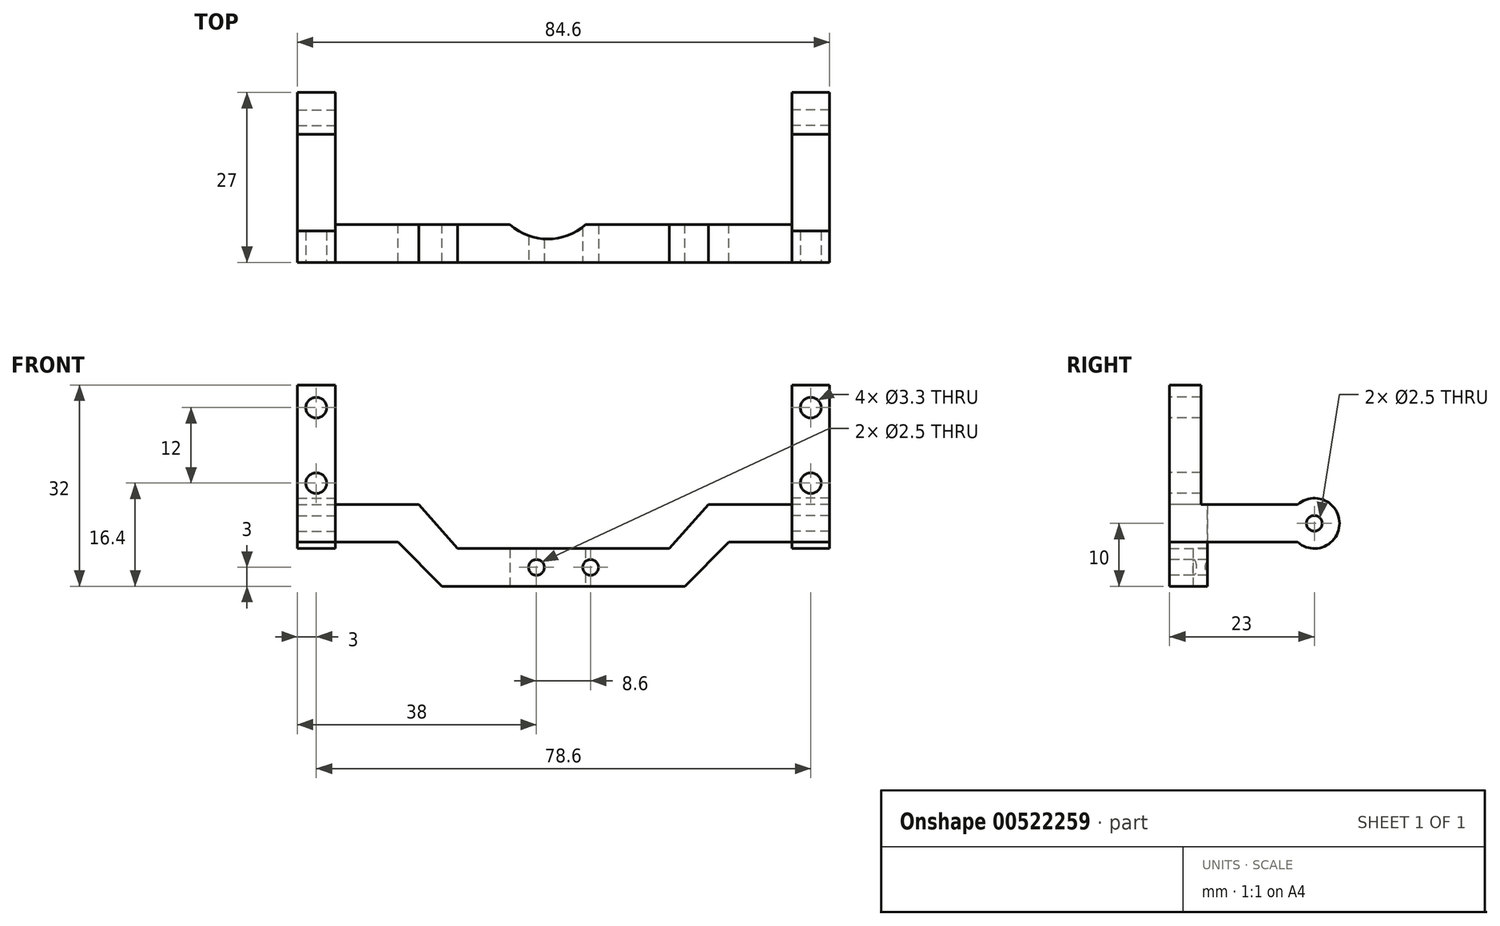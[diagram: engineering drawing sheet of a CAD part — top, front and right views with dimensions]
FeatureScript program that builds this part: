
annotation { "Feature Type Name" : "Feature", "Feature Type Description" : "" }
export const myFeature = defineFeature(function(context is Context, id is Id, definition is map)
    precondition{}
    {
        {
            var Q0;
            Q0=qCreatedBy(makeId("Top.planeOp"),FACE);
            var sketch = newSketch(context, id + "F0", { "sketchPlane" : qUnion([Q0])});
            skLineSegment(sketch, "E0.bottom", {"start": v(-33.8, 3) * mm, "end": v(38.8, 3) * mm});
            skLineSegment(sketch, "E0.top", {"start": v(-33.8, -3) * mm, "end": v(-6, -3) * mm});
            skLineSegment(sketch, "E0.left", {"start": v(-33.8, 3) * mm, "end": v(-33.8, -3) * mm});
            skLineSegment(sketch, "E0.right", {"start": v(38.8, 3) * mm, "end": v(38.8, -3) * mm});
            skLineSegment(sketch, "E1.trimOffspring", {"start": v(6, -3) * mm, "end": v(38.8, -3) * mm});
            skLineSegment(sketch, "E2", {"start": v(-6, -3) * mm, "end": v(6, -3) * mm});
            skSolve(sketch);
        }
        {
            var Q0;
            Q0=makeQuery(id+"F0.imprint","IMPRINT",FACE,{"disambiguationData":[TD([[makeQuery(id+"F0.imprint","IMPRINT",EDGE,{"derivedFrom":sQuery(id+"F0.wireOp",EDGE,"E0.bottom")}),-1.0]])]});
            extrude(context, id + "F1", {"entities" : qUnion([Q0]), "depth" : 13 * mm, "offsetDistance" : 25 * mm});
        }
        {
            var Q0;
            Q0=makeQuery(id+"F1.opExtrude","SWEPT_FACE",FACE,{"disambiguationData":[OSD([sQuery(id+"F0.wireOp",EDGE,"E0.bottom")])]});
            var sketch = newSketch(context, id + "F2", { "sketchPlane" : qUnion([Q0])});
            skLineSegment(sketch, "E3", {"start": v(-38.8, 0) * mm, "end": v(33.8, 0) * mm});
            skLineSegment(sketch, "E4", {"start": v(33.8, 0) * mm, "end": v(33.8, 13) * mm});
            skLineSegment(sketch, "E5", {"start": v(33.8, 13) * mm, "end": v(-38.8, 13) * mm});
            skLineSegment(sketch, "E6", {"start": v(-38.8, 13) * mm, "end": v(-38.8, 0) * mm});
            skLineSegment(sketch, "E7", {"start": v(-38.8, 7) * mm, "end": v(-28.8, 7) * mm});
            skLineSegment(sketch, "E8", {"start": v(-28.8, 7) * mm, "end": v(-28.8, 0) * mm});
            skLineSegment(sketch, "E9", {"start": v(23.8, 7) * mm, "end": v(23.8, 0) * mm});
            skLineSegment(sketch, "E10", {"start": v(-28.8, 7) * mm, "end": v(-21.8, 0) * mm});
            skLineSegment(sketch, "E11", {"start": v(23.8, 7) * mm, "end": v(16.8, 0) * mm});
            skLineSegment(sketch, "E12.trimOffspring", {"start": v(23.8, 7) * mm, "end": v(33.8, 7) * mm});
            skLineSegment(sketch, "E13.0", {"start": v(-24.56, 11.24) * mm, "end": v(-20.28, 6.97) * mm});
            skLineSegment(sketch, "E14.0", {"start": v(19.56, 11.24) * mm, "end": v(14.31, 6) * mm});
            skLineSegment(sketch, "E15", {"start": v(-19.31, 6) * mm, "end": v(14.31, 6) * mm});
            skPoint(sketch, "E15.startSnap0", {"position": v(-20.28, 6.97) * mm});
            skPoint(sketch, "E16.orphan", {"position": v(-27.25, 13.94) * mm});
            skPoint(sketch, "E17.orphan", {"position": v(-19.34, -2.46) * mm});
            skPoint(sketch, "E18.orphan", {"position": v(14.34, -2.46) * mm});
            skPoint(sketch, "E19.orphan", {"position": v(6.71, 0) * mm});
            skLineSegment(sketch, "E20.trimOffspring", {"start": v(-19.31, 6) * mm, "end": v(-25.51, 13) * mm});
            skPoint(sketch, "E21.end.orphan", {"position": v(-13.31, 0) * mm});
            skLineSegment(sketch, "E22.trimOffspring", {"start": v(14.31, 6) * mm, "end": v(20.51, 13) * mm});
            skPoint(sketch, "E23.orphan", {"position": v(-20.28, 6) * mm});
            skSolve(sketch);
        }
        {
            var Q0;
            {var subQ0=sQuery(id+"F2.wireOp",EDGE,"E8");Q0=makeQuery(id+"F2.imprint","IMPRINT",FACE,{"disambiguationData":[TD([[makeQuery(id+"F2.imprint","IMPRINT",EDGE,{"derivedFrom":subQ0}),1.0]])]});}
            var Q1;
            {var subQ4=sQuery(id+"F2.wireOp",EDGE,"E7");Q1=makeQuery(id+"F2.imprint","IMPRINT",FACE,{"disambiguationData":[TD([[makeQuery(id+"F2.imprint","IMPRINT",EDGE,{"derivedFrom":subQ4}),-1.0]])]});}
            var Q2;
            {var subQ3=sQuery(id+"F2.wireOp",EDGE,"E15");Q2=makeQuery(id+"F2.imprint","IMPRINT",FACE,{"disambiguationData":[TD([[makeQuery(id+"F2.imprint","IMPRINT",EDGE,{"derivedFrom":subQ3}),1.0]])]});}
            var Q3;
            {var subQ0=sQuery(id+"F2.wireOp",EDGE,"E9");Q3=makeQuery(id+"F2.imprint","IMPRINT",FACE,{"disambiguationData":[TD([[makeQuery(id+"F2.imprint","IMPRINT",EDGE,{"derivedFrom":subQ0}),-1.0]])]});}
            var Q4;
            {var subQ3=sQuery(id+"F2.wireOp",EDGE,"E9");Q4=makeQuery(id+"F2.imprint","IMPRINT",FACE,{"disambiguationData":[TD([[makeQuery(id+"F2.imprint","IMPRINT",EDGE,{"derivedFrom":subQ3}),1.0]])]});}
            extrude(context, id + "F3", {"entities" : qUnion([Q0, Q1, Q2, Q3, Q4]), "operationType" : NewBodyOperationType.REMOVE, "endBound" : BoundingType.THROUGH_ALL, "oppositeDirection" : true, "depth" : 25 * mm, "offsetDistance" : 25 * mm});
        }
        {
            var Q0;
            Q0=makeQuery(id+"F1.opExtrude","CAP_FACE",FACE,{"disambiguationData":[OSD([sQuery(id+"F0.wireOp",EDGE,"E0.bottom"),sQuery(id+"F0.wireOp",EDGE,"E0.top"),sQuery(id+"F0.wireOp",EDGE,"E0.left"),sQuery(id+"F0.wireOp",EDGE,"E0.right"),sQuery(id+"F0.wireOp",EDGE,"E1.trimOffspring"),sQuery(id+"F0.wireOp",EDGE,"E2")])],"isStart":true});
            var sketch = newSketch(context, id + "F4", { "sketchPlane" : qUnion([Q0])});
            skArc(sketch, "E24", {"start": v(6, -3) * mm, "mid": v(0, -0.7) * mm, "end": v(-6, -3) * mm});
            skSolve(sketch);
        }
        {
            var Q0;
            {var subQ0=sQuery(id+"F4.wireOp",EDGE,"E24");Q0=makeQuery(id+"F4.imprint","IMPRINT",FACE,{"disambiguationData":[TD([[makeQuery(id+"F4.imprint","IMPRINT",EDGE,{"derivedFrom":subQ0}),1.0]])]});}
            extrude(context, id + "F5", {"entities" : qUnion([Q0]), "operationType" : NewBodyOperationType.REMOVE, "endBound" : BoundingType.THROUGH_ALL, "oppositeDirection" : true, "depth" : 25 * mm, "offsetDistance" : 25 * mm});
        }
        {
            var Q0;
            Q0=makeQuery(id+"F1.opExtrude","SWEPT_FACE",FACE,{"disambiguationData":[OSD([sQuery(id+"F0.wireOp",EDGE,"E0.top"),sQuery(id+"F0.wireOp",EDGE,"E1.trimOffspring"),sQuery(id+"F0.wireOp",EDGE,"E2")])]});
            var sketch = newSketch(context, id + "F6", { "sketchPlane" : qUnion([Q0])});
            skCircle(sketch, "E25", {"center": v(-1.8, 3) * mm, "radius": 1.25 * mm});
            skCircle(sketch, "E26", {"center": v(6.8, 3) * mm, "radius": 1.25 * mm});
            skSolve(sketch);
        }
        {
            var Q0;
            Q0=makeQuery(id+"F6.imprint","IMPRINT",FACE,{"disambiguationData":[TD([[makeQuery(id+"F6.imprint","IMPRINT",EDGE,{"derivedFrom":sQuery(id+"F6.wireOp",EDGE,"E25")}),1.0]])]});
            var Q1;
            Q1=makeQuery(id+"F6.imprint","IMPRINT",FACE,{"disambiguationData":[TD([[makeQuery(id+"F6.imprint","IMPRINT",EDGE,{"derivedFrom":sQuery(id+"F6.wireOp",EDGE,"E26")}),1.0]])]});
            extrude(context, id + "F7", {"entities" : qUnion([Q0, Q1]), "operationType" : NewBodyOperationType.REMOVE, "endBound" : BoundingType.THROUGH_ALL, "oppositeDirection" : true, "depth" : 25 * mm, "offsetDistance" : 25 * mm});
        }
        {
            var Q0;
            Q0=makeQuery(id+"F1.opExtrude","SWEPT_FACE",FACE,{"disambiguationData":[OSD([sQuery(id+"F0.wireOp",EDGE,"E0.right")])]});
            var sketch = newSketch(context, id + "F8", { "sketchPlane" : qUnion([Q0])});
            skLineSegment(sketch, "E27", {"start": v(-3, 7) * mm, "end": v(-3, 32) * mm});
            skLineSegment(sketch, "E28", {"start": v(2, 32) * mm, "end": v(2, 13) * mm});
            skLineSegment(sketch, "E29", {"start": v(-3, 32) * mm, "end": v(2, 32) * mm});
            skLineSegment(sketch, "E30", {"start": v(2, 13) * mm, "end": v(17.35, 13) * mm});
            skLineSegment(sketch, "E31", {"start": v(17.35, 7) * mm, "end": v(3, 7) * mm});
            skPoint(sketch, "E32.orphan", {"position": v(-3, 31.12) * mm});
            skPoint(sketch, "E33.orphan", {"position": v(2, 31.12) * mm});
            skCircle(sketch, "E34", {"center": v(20, 10) * mm, "radius": 1.25 * mm});
            skPoint(sketch, "E34.centerSnap0", {"position": v(3, 10) * mm});
            skArc(sketch, "E35", {"start": v(17.35, 7) * mm, "mid": v(24, 10) * mm, "end": v(17.35, 13) * mm});
            skPoint(sketch, "E36.orphan", {"position": v(30, 7) * mm});
            skLineSegment(sketch, "E37", {"start": v(3, 7) * mm, "end": v(-3, 7) * mm});
            skLineSegment(sketch, "E38", {"start": v(-3, 13) * mm, "end": v(-3, 7) * mm});
            skLineSegment(sketch, "E39", {"start": v(2, 13) * mm, "end": v(3, 13) * mm});
            skSolve(sketch);
        }
        {
            var Q0;
            Q0=makeQuery(id+"F8.imprint","IMPRINT",FACE,{"disambiguationData":[TD([[makeQuery(id+"F8.imprint","IMPRINT",EDGE,{"derivedFrom":sQuery(id+"F8.wireOp",EDGE,"E31")}),-1.0]])]});
            var Q1;
            {var subQ4=sQuery(id+"F8.wireOp",EDGE,"E28");Q1=makeQuery(id+"F8.imprint","IMPRINT",FACE,{"disambiguationData":[TD([[makeQuery(id+"F8.imprint","IMPRINT",EDGE,{"derivedFrom":subQ4}),-1.0]])]});}
            var Q2;
            Q2=makeQuery(id+"F8.imprint","IMPRINT",FACE,{"disambiguationData":[TD([[makeQuery(id+"F8.imprint","IMPRINT",EDGE,{"derivedFrom":sQuery(id+"F8.wireOp",EDGE,"E37")}),1.0]])]});
            extrude(context, id + "F9", {"entities" : qUnion([Q0, Q1, Q2]), "depth" : 6 * mm, "offsetDistance" : 25 * mm});
        }
        {
            var Q0;
            Q0=makeQuery(id+"F9.opExtrude","SWEPT_FACE",FACE,{"disambiguationData":[OSD([sQuery(id+"F8.wireOp",EDGE,"E27")])]});
            var sketch = newSketch(context, id + "F10", { "sketchPlane" : qUnion([Q0])});
            skCircle(sketch, "E40", {"center": v(41.8, 28.4) * mm, "radius": 1.65 * mm});
            skCircle(sketch, "E41", {"center": v(41.8, 16.4) * mm, "radius": 1.65 * mm});
            skSolve(sketch);
        }
        {
            var Q0;
            Q0=makeQuery(id+"F10.imprint","IMPRINT",FACE,{"disambiguationData":[TD([[makeQuery(id+"F10.imprint","IMPRINT",EDGE,{"derivedFrom":sQuery(id+"F10.wireOp",EDGE,"E41")}),1.0]])]});
            var Q1;
            Q1=makeQuery(id+"F10.imprint","IMPRINT",FACE,{"disambiguationData":[TD([[makeQuery(id+"F10.imprint","IMPRINT",EDGE,{"derivedFrom":sQuery(id+"F10.wireOp",EDGE,"E40")}),1.0]])]});
            extrude(context, id + "F11", {"entities" : qUnion([Q0, Q1]), "operationType" : NewBodyOperationType.REMOVE, "endBound" : BoundingType.THROUGH_ALL, "oppositeDirection" : true, "depth" : 25 * mm, "offsetDistance" : 25 * mm});
        }
        {
            var Q0;
            Q0=makeQuery(id+"F1.opExtrude","SWEPT_FACE",FACE,{"disambiguationData":[OSD([sQuery(id+"F0.wireOp",EDGE,"E0.left")])]});
            var sketch = newSketch(context, id + "F12", { "sketchPlane" : qUnion([Q0])});
            skLineSegment(sketch, "E42", {"start": v(3, 13) * mm, "end": v(3, 32) * mm});
            skLineSegment(sketch, "E43", {"start": v(-3, 13) * mm, "end": v(-17.35, 13) * mm});
            skLineSegment(sketch, "E44", {"start": v(-3, 7) * mm, "end": v(-17.35, 7) * mm});
            skLineSegment(sketch, "E45", {"start": v(-30, 4) * mm, "end": v(-30.87, 4) * mm});
            skArc(sketch, "E46", {"start": v(-17.35, 13) * mm, "mid": v(-24, 10) * mm, "end": v(-17.35, 7) * mm});
            skCircle(sketch, "E47", {"center": v(-20, 10) * mm, "radius": 1.25 * mm});
            skLineSegment(sketch, "E48", {"start": v(3, 32) * mm, "end": v(-2, 32) * mm});
            skLineSegment(sketch, "E49", {"start": v(-2, 13) * mm, "end": v(-2, 32) * mm});
            skLineSegment(sketch, "E50", {"start": v(3, 13) * mm, "end": v(3, 7) * mm});
            skLineSegment(sketch, "E51", {"start": v(3, 7) * mm, "end": v(-3, 7) * mm});
            skLineSegment(sketch, "E52", {"start": v(-3, 13) * mm, "end": v(-2, 13) * mm});
            skSolve(sketch);
        }
        {
            var Q0;
            Q0=makeQuery(id+"F12.imprint","IMPRINT",FACE,{"disambiguationData":[TD([[makeQuery(id+"F12.imprint","IMPRINT",EDGE,{"derivedFrom":sQuery(id+"F12.wireOp",EDGE,"E42")}),1.0]])]});
            var Q1;
            Q1=makeQuery(id+"F12.imprint","IMPRINT",FACE,{"disambiguationData":[TD([[makeQuery(id+"F12.imprint","IMPRINT",EDGE,{"derivedFrom":sQuery(id+"F12.wireOp",EDGE,"E43")}),1.0]])]});
            var Q2;
            {var subQ0=sQuery(id+"F12.wireOp",EDGE,"E50");Q2=makeQuery(id+"F12.imprint","IMPRINT",FACE,{"disambiguationData":[TD([[makeQuery(id+"F12.imprint","IMPRINT",EDGE,{"derivedFrom":subQ0}),-1.0]])]});}
            extrude(context, id + "F13", {"entities" : qUnion([Q0, Q1, Q2]), "depth" : 6 * mm, "offsetDistance" : 25 * mm});
        }
        {
            var Q0;
            Q0=makeQuery(id+"F13.opExtrude","SWEPT_FACE",FACE,{"disambiguationData":[OSD([sQuery(id+"F12.wireOp",EDGE,"E42")])]});
            var sketch = newSketch(context, id + "F14", { "sketchPlane" : qUnion([Q0])});
            skCircle(sketch, "E53", {"center": v(-36.8, 28.4) * mm, "radius": 1.65 * mm});
            skCircle(sketch, "E54", {"center": v(-36.8, 16.4) * mm, "radius": 1.65 * mm});
            skSolve(sketch);
        }
        {
            var Q0;
            Q0=makeQuery(id+"F14.imprint","IMPRINT",FACE,{"disambiguationData":[TD([[makeQuery(id+"F14.imprint","IMPRINT",EDGE,{"derivedFrom":sQuery(id+"F14.wireOp",EDGE,"E53")}),1.0]])]});
            var Q1;
            Q1=makeQuery(id+"F14.imprint","IMPRINT",FACE,{"disambiguationData":[TD([[makeQuery(id+"F14.imprint","IMPRINT",EDGE,{"derivedFrom":sQuery(id+"F14.wireOp",EDGE,"E54")}),1.0]])]});
            extrude(context, id + "F15", {"entities" : qUnion([Q0, Q1]), "operationType" : NewBodyOperationType.REMOVE, "endBound" : BoundingType.THROUGH_ALL, "oppositeDirection" : true, "depth" : 25 * mm, "offsetDistance" : 25 * mm});
        }
    });
